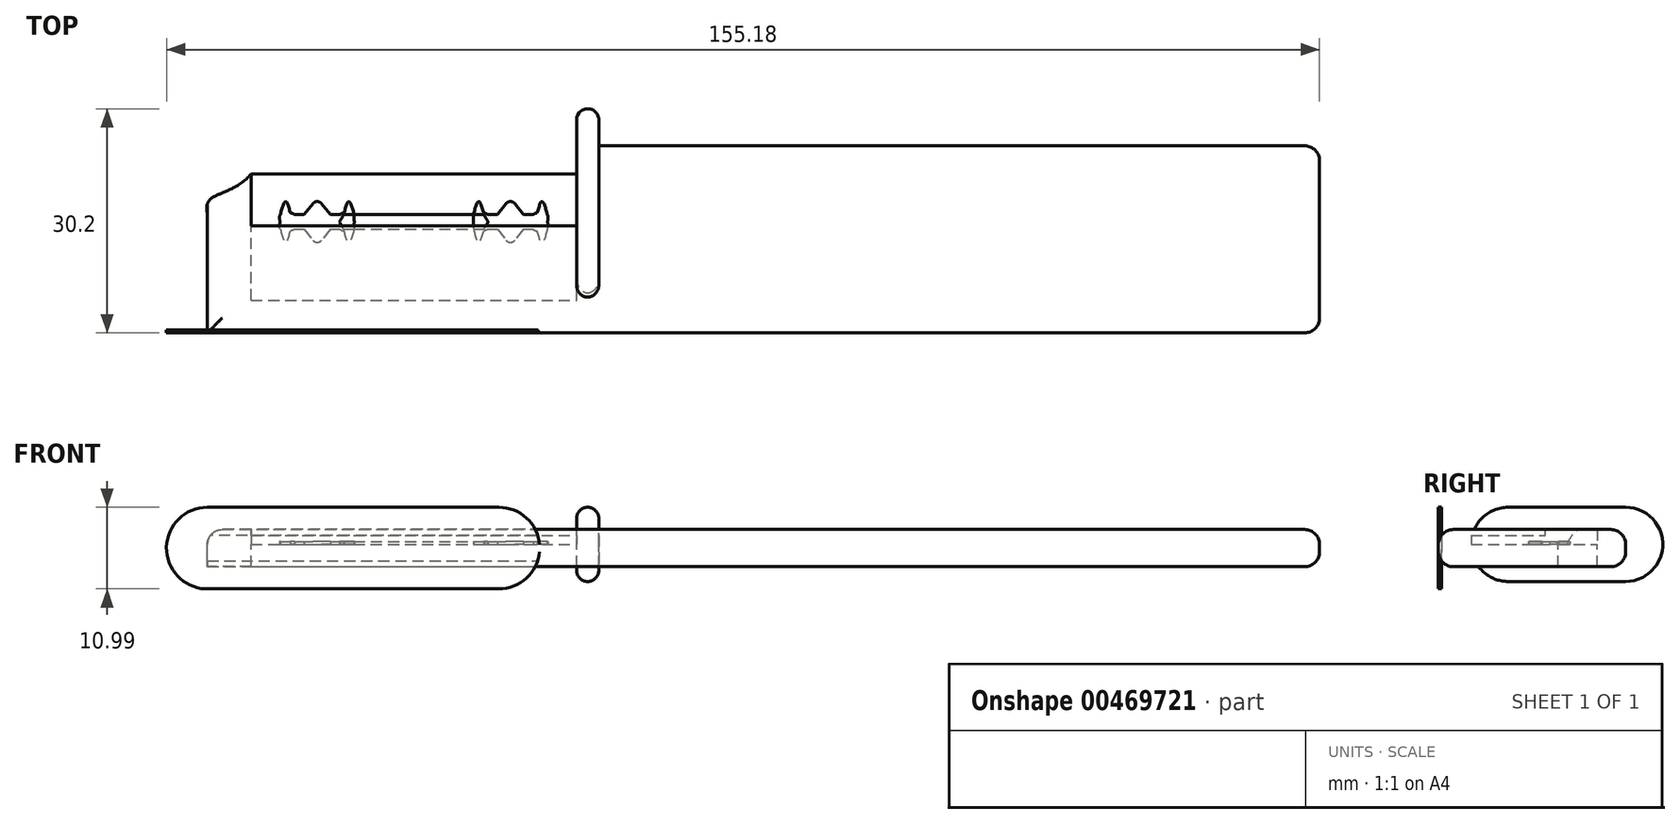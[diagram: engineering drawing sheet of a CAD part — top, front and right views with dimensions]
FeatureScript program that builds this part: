
annotation { "Feature Type Name" : "Feature", "Feature Type Description" : "" }
export const myFeature = defineFeature(function(context is Context, id is Id, definition is map)
    precondition{}
    {
        {
            var Q0;
            Q0=qCreatedBy(makeId("Top.planeOp"),FACE);
            var sketch = newSketch(context, id + "F0", { "sketchPlane" : qUnion([Q0])});
            skLineSegment(sketch, "E0", {"start": v(-36, 0) * mm, "end": v(0, 0) * mm});
            skLineSegment(sketch, "E1", {"start": v(-36, 1) * mm, "end": v(0, 1) * mm});
            skLineSegment(sketch, "E2.MirrorCS", {"start": v(-36, 2) * mm, "end": v(0, 2) * mm});
            skPoint(sketch, "E3", {"position": v(-31, 3.75) * mm});
            skPoint(sketch, "E4.MirrorP", {"position": v(-31, -1.75) * mm});
            skLineSegment(sketch, "E5", {"start": v(-31, 3.75) * mm, "end": v(-31, -1.75) * mm});
            skArc(sketch, "E6", {"start": v(-30.41, 3.47) * mm, "mid": v(-31, 3.75) * mm, "end": v(-31.59, 3.47) * mm});
            skLineSegment(sketch, "E7", {"start": v(-32.75, 2) * mm, "end": v(-31.59, 3.47) * mm});
            skPoint(sketch, "E8", {"position": v(-31.59, 3.47) * mm});
            skPoint(sketch, "E9", {"position": v(-30.41, 3.47) * mm});
            skLineSegment(sketch, "E10", {"start": v(-18, -5.38) * mm, "end": v(-18, 16.22) * mm});
            skFitSpline(sketch, "E11", {"points": [v(-35.93, 2) * mm, v(-35.23, 3.75) * mm, v(-34.53, 2) * mm, v(-34, 1) * mm, v(-34.07, 0) * mm, v(-35.93, 0) * mm, v(-36, 1) * mm, v(-35.93, 2) * mm]});
            skFitSpline(sketch, "E12.MirrorCS", {"points": [v(-35.93, 0) * mm, v(-35.23, -1.75) * mm, v(-34.53, 0) * mm, v(-34, 1) * mm, v(-34.07, 2) * mm, v(-35.93, 2) * mm, v(-36, 1) * mm, v(-35.93, 0) * mm]});
            skLineSegment(sketch, "E13.MirrorCS", {"start": v(-29.25, 2) * mm, "end": v(-30.41, 3.47) * mm});
            skLineSegment(sketch, "E14.MirrorCS", {"start": v(-32.75, 0) * mm, "end": v(-31.59, -1.47) * mm});
            skArc(sketch, "E15.MirrorCS", {"start": v(-30.41, -1.47) * mm, "mid": v(-31, -1.75) * mm, "end": v(-31.59, -1.47) * mm});
            skLineSegment(sketch, "E16.MirrorCS", {"start": v(-29.25, 0) * mm, "end": v(-30.41, -1.47) * mm});
            skFitSpline(sketch, "E17.MirrorCS", {"points": [v(-26.07, 2) * mm, v(-26.77, 3.75) * mm, v(-27.47, 2) * mm, v(-28, 1) * mm, v(-27.93, 0) * mm, v(-26.07, 0) * mm, v(-26, 1) * mm, v(-26.07, 2) * mm]});
            skFitSpline(sketch, "E18.MirrorCS", {"points": [v(-26.07, 0) * mm, v(-26.77, -1.75) * mm, v(-27.47, 0) * mm, v(-28, 1) * mm, v(-27.93, 2) * mm, v(-26.07, 2) * mm, v(-26, 1) * mm, v(-26.07, 0) * mm]});
            skFitSpline(sketch, "E19.MirrorCS", {"points": [v(-0.07, 2) * mm, v(-0.77, 3.75) * mm, v(-1.47, 2) * mm, v(-2, 1) * mm, v(-1.93, 0) * mm, v(-0.07, 0) * mm, v(0, 1) * mm, v(-0.07, 2) * mm]});
            skFitSpline(sketch, "E20.MirrorCS", {"points": [v(-0.07, 0) * mm, v(-0.77, -1.75) * mm, v(-1.47, 0) * mm, v(-2, 1) * mm, v(-1.93, 2) * mm, v(-0.07, 2) * mm, v(0, 1) * mm, v(-0.07, 0) * mm]});
            skLineSegment(sketch, "E21.MirrorCS", {"start": v(-3.25, 2) * mm, "end": v(-4.41, 3.47) * mm});
            skArc(sketch, "E22.MirrorCS", {"start": v(-5.59, 3.47) * mm, "mid": v(-5, 3.75) * mm, "end": v(-4.41, 3.47) * mm});
            skArc(sketch, "E23.MirrorCS", {"start": v(-5.59, -1.47) * mm, "mid": v(-5, -1.75) * mm, "end": v(-4.41, -1.47) * mm});
            skLineSegment(sketch, "E24.MirrorCS", {"start": v(-3.25, 0) * mm, "end": v(-4.41, -1.47) * mm});
            skLineSegment(sketch, "E25.MirrorCS", {"start": v(-6.75, 2) * mm, "end": v(-5.59, 3.47) * mm});
            skLineSegment(sketch, "E26.MirrorCS", {"start": v(-6.75, 0) * mm, "end": v(-5.59, -1.47) * mm});
            skFitSpline(sketch, "E27.MirrorCS", {"points": [v(-9.93, 2) * mm, v(-9.23, 3.75) * mm, v(-8.53, 2) * mm, v(-8, 1) * mm, v(-8.07, 0) * mm, v(-9.93, 0) * mm, v(-10, 1) * mm, v(-9.93, 2) * mm]});
            skFitSpline(sketch, "E28.MirrorCS", {"points": [v(-9.93, 0) * mm, v(-9.23, -1.75) * mm, v(-8.53, 0) * mm, v(-8, 1) * mm, v(-8.07, 2) * mm, v(-9.93, 2) * mm, v(-10, 1) * mm, v(-9.93, 0) * mm]});
            skSolve(sketch);
        }
        {
            var Q0;
            Q0 = qSketchRegion(id + "F0", true);
            extrude(context, id + "F1", {"entities" : qUnion([Q0]), "depth" : .4 * mm, "offsetDistance" : 25 * mm});
        }
        {
            var Q0;
            Q0=makeQuery(id+"F1.opExtrude","CAP_FACE",FACE,{"disambiguationData":[OSD([sQuery(id+"F0.wireOp",EDGE,"E0"),sQuery(id+"F0.wireOp",EDGE,"E2.MirrorCS"),sQuery(id+"F0.wireOp",EDGE,"E6"),sQuery(id+"F0.wireOp",EDGE,"E7"),sQuery(id+"F0.wireOp",EDGE,"E11"),sQuery(id+"F0.wireOp",EDGE,"E12.MirrorCS"),sQuery(id+"F0.wireOp",EDGE,"E13.MirrorCS"),sQuery(id+"F0.wireOp",EDGE,"E14.MirrorCS"),sQuery(id+"F0.wireOp",EDGE,"E15.MirrorCS"),sQuery(id+"F0.wireOp",EDGE,"E16.MirrorCS"),sQuery(id+"F0.wireOp",EDGE,"E17.MirrorCS"),sQuery(id+"F0.wireOp",EDGE,"E18.MirrorCS"),sQuery(id+"F0.wireOp",EDGE,"E19.MirrorCS"),sQuery(id+"F0.wireOp",EDGE,"E20.MirrorCS"),sQuery(id+"F0.wireOp",EDGE,"E21.MirrorCS"),sQuery(id+"F0.wireOp",EDGE,"E22.MirrorCS"),sQuery(id+"F0.wireOp",EDGE,"E23.MirrorCS"),sQuery(id+"F0.wireOp",EDGE,"E24.MirrorCS"),sQuery(id+"F0.wireOp",EDGE,"E25.MirrorCS"),sQuery(id+"F0.wireOp",EDGE,"E26.MirrorCS"),sQuery(id+"F0.wireOp",EDGE,"E27.MirrorCS"),sQuery(id+"F0.wireOp",EDGE,"E28.MirrorCS")])],"isStart":true});
            var sketch = newSketch(context, id + "F2", { "sketchPlane" : qUnion([Q0])});
            skLineSegment(sketch, "E29", {"start": v(-39.9, -7.45) * mm, "end": v(3.9, -7.45) * mm});
            skLineSegment(sketch, "E30", {"start": v(-39.9, 9.55) * mm, "end": v(3.9, 9.55) * mm});
            skLineSegment(sketch, "E31", {"start": v(-39.9, 9.55) * mm, "end": v(-39.9, -7.45) * mm});
            skLineSegment(sketch, "E32", {"start": v(3.9, 9.55) * mm, "end": v(3.9, -7.45) * mm});
            skLineSegment(sketch, "E33", {"start": v(3.9, -11.25) * mm, "end": v(103.9, -11.25) * mm});
            skLineSegment(sketch, "E34", {"start": v(-39.6, 13.55) * mm, "end": v(103.9, 13.55) * mm});
            skLineSegment(sketch, "E35", {"start": v(103.9, -11.25) * mm, "end": v(103.9, 13.55) * mm});
            skLineSegment(sketch, "E36", {"start": v(-39.6, 13.55) * mm, "end": v(-45.78, 13.55) * mm});
            skLineSegment(sketch, "E37", {"start": v(-45.78, 13.55) * mm, "end": v(-45.78, -3.45) * mm});
            skFitSpline(sketch, "E38", {"points": [v(-39.9, -7.45) * mm, v(-45.78, -3.45) * mm, v(-39.9, 5.9) * mm], "startDerivative": vector(-14.74, 17.67) * mm, "endDerivative": vector(17.5, 14.8) * mm});
            skLineSegment(sketch, "E39", {"start": v(3.9, -7.45) * mm, "end": v(3.9, -11.25) * mm});
            skSolve(sketch);
        }
        {
            var Q0;
            Q0 = qSketchRegion(id + "F2", true);
            extrude(context, id + "F3", {"entities" : qUnion([Q0]), "operationType" : NewBodyOperationType.ADD, "depth" : 3 * mm});
        }
        {
            var Q0;
            Q0=makeQuery(id+"F2.imprint","IMPRINT",FACE,{"disambiguationData":[TD([[makeQuery(id+"F2.imprint","IMPRINT",EDGE,{"derivedFrom":sQuery(id+"F2.wireOp",EDGE,"E30")}),1.0]])]});
            var Q1;
            Q1=makeQuery(id+"F2.imprint","IMPRINT",FACE,{"disambiguationData":[TD([[makeQuery(id+"F2.imprint","IMPRINT",EDGE,{"derivedFrom":sQuery(id+"F2.wireOp",EDGE,"E31")}),-1.0]])]});
            extrude(context, id + "F4", {"entities" : qUnion([Q0, Q1]), "operationType" : NewBodyOperationType.ADD, "oppositeDirection" : true, "depth" : 2 * mm});
        }
        {
            var Q0;
            Q0=makeQuery(id+"F4.opExtrude","CAP_FACE",FACE,{"disambiguationData":[OSD([sQuery(id+"F2.wireOp",EDGE,"E30"),sQuery(id+"F2.wireOp",EDGE,"E31"),sQuery(id+"F2.wireOp",EDGE,"E32"),sQuery(id+"F2.wireOp",EDGE,"E33"),sQuery(id+"F2.wireOp",EDGE,"8b2e560c-d758-45f4-89a4-b663eee040c1"),sQuery(id+"F2.wireOp",EDGE,"E34"),sQuery(id+"F2.wireOp",EDGE,"E35"),sQuery(id+"F2.wireOp",EDGE,"E36"),sQuery(id+"F2.wireOp",EDGE,"E37"),sQuery(id+"F2.wireOp",EDGE,"c306e02f-bcff-4e16-9162-90af26744d23")])],"isStart":false});
            var sketch = newSketch(context, id + "F5", { "sketchPlane" : qUnion([Q0])});
            skLineSegment(sketch, "E40.bottom", {"start": v(3.9, -9.55) * mm, "end": v(-39.9, -9.55) * mm});
            skLineSegment(sketch, "E40.top", {"start": v(3.9, 0.45) * mm, "end": v(-39.9, 0.45) * mm});
            skLineSegment(sketch, "E40.left", {"start": v(3.9, -9.55) * mm, "end": v(3.9, 0.45) * mm});
            skLineSegment(sketch, "E40.right", {"start": v(-39.9, -9.55) * mm, "end": v(-39.9, 0.45) * mm});
            skSolve(sketch);
        }
        {
            var Q0;
            Q0 = qSketchRegion(id + "F5", true);
            extrude(context, id + "F6", {"entities" : qUnion([Q0]), "operationType" : NewBodyOperationType.ADD, "oppositeDirection" : true, "depth" : .8 * mm});
        }
        {
            var Q0;
            {var subQ0=sQuery(id+"F2.wireOp",EDGE,"E36");var subQ1=sQuery(id+"F2.wireOp",EDGE,"E34");Q0=makeQuery(id+"F4.boolean.opBoolean","MERGE",FACE,{"derivedFrom":[makeQuery(id+"F3.opExtrude","SWEPT_FACE",FACE,{"disambiguationData":[OSD([subQ1,subQ0])]}),makeQuery(id+"F4.opExtrude","SWEPT_FACE",FACE,{"disambiguationData":[OSD([subQ1,subQ0])]})]});}
            var sketch = newSketch(context, id + "F7", { "sketchPlane" : qUnion([Q0])});
            skLineSegment(sketch, "E41.bottom", {"start": v(-45.78, 2) * mm, "end": v(103.9, 2) * mm});
            skLineSegment(sketch, "E41.top", {"start": v(-45.78, -3) * mm, "end": v(103.9, -3) * mm});
            skLineSegment(sketch, "E41.left", {"start": v(-45.78, 2) * mm, "end": v(-45.78, -3) * mm});
            skLineSegment(sketch, "E41.right", {"start": v(103.9, 2) * mm, "end": v(103.9, -3) * mm});
            skLineSegment(sketch, "E42", {"start": v(-6.54, 5) * mm, "end": v(-45.78, 5) * mm});
            skLineSegment(sketch, "E43.MirrorCS", {"start": v(-6.54, -6) * mm, "end": v(-46.03, -6) * mm});
            skArc(sketch, "E44", {"start": v(-45.78, 5) * mm, "mid": v(-51.28, -0.38) * mm, "end": v(-46.03, -6) * mm});
            skArc(sketch, "E45", {"start": v(-6.54, -6) * mm, "mid": v(-3.67, -5.19) * mm, "end": v(-1.65, -3) * mm});
            skArc(sketch, "E46.trimOffspring", {"start": v(-1.65, 2) * mm, "mid": v(-3.67, 4.2) * mm, "end": v(-6.54, 5) * mm});
            skSolve(sketch);
        }
        {
            var Q0;
            Q0 = qSketchRegion(id + "F7", true);
            extrude(context, id + "F8", {"entities" : qUnion([Q0]), "operationType" : NewBodyOperationType.ADD, "depth" : .4 * mm});
        }
        {
            var Q0;
            {var subQ0=sQuery(id+"F2.wireOp",EDGE,"E35");var subQ1=sQuery(id+"F2.wireOp",EDGE,"E33");Q0=makeQuery(id+"F4.boolean.opBoolean","MERGE",EDGE,{"derivedFrom":[makeQuery(id+"F3.opExtrude","SWEPT_EDGE",EDGE,{"disambiguationData":[OSD([subQ1,subQ0])]}),makeQuery(id+"F4.opExtrude","SWEPT_EDGE",EDGE,{"disambiguationData":[OSD([subQ1,subQ0])]})]});}
            fillet(context, id + "F9", {"entities" : qUnion([Q0]), "radius" : 2 * mm, "tangentPropagation" : true, "allowEdgeOverflow" : false});
        }
        {
            var Q0;
            Q0=makeQuery(id+"F8.opExtrude","CAP_EDGE",EDGE,{"disambiguationData":[OSD([sQuery(id+"F7.wireOp",EDGE,"E41.right")])],"isStart":false});
            fillet(context, id + "F10", {"entities" : qUnion([Q0]), "radius" : 2 * mm, "tangentPropagation" : true, "allowEdgeOverflow" : false});
        }
        {
            var Q0;
            Q0=makeQuery(id+"F4.opExtrude","CAP_EDGE",EDGE,{"disambiguationData":[OSD([sQuery(id+"F2.wireOp",EDGE,"E33")])],"isStart":false});
            fillet(context, id + "F11", {"entities" : qUnion([Q0]), "radius" : 2 * mm, "tangentPropagation" : true, "allowEdgeOverflow" : false});
        }
        {
            var Q0;
            Q0=makeQuery(id+"F3.opExtrude","CAP_EDGE",EDGE,{"disambiguationData":[OSD([sQuery(id+"F2.wireOp",EDGE,"E33")])],"isStart":false});
            fillet(context, id + "F12", {"entities" : qUnion([Q0]), "radius" : 2 * mm, "tangentPropagation" : true, "allowEdgeOverflow" : false});
        }
        {
            var Q0;
            Q0=makeQuery(id+"F4.opExtrude","CAP_EDGE",EDGE,{"disambiguationData":[OSD([sQuery(id+"F2.wireOp",EDGE,"E37")])],"isStart":false});
            fillet(context, id + "F13", {"entities" : qUnion([Q0]), "radius" : 2 * mm, "tangentPropagation" : true, "allowEdgeOverflow" : false});
        }
        {
            var Q0;
            {var subQ0=sQuery(id+"F2.wireOp",EDGE,"E39");Q0=makeQuery(id+"F4.boolean.opBoolean","MERGE",FACE,{"derivedFrom":[makeQuery(id+"F3.opExtrude","SWEPT_FACE",FACE,{"disambiguationData":[OSD([subQ0])]}),makeQuery(id+"F4.opExtrude","SWEPT_FACE",FACE,{"disambiguationData":[OSD([sQuery(id+"F2.wireOp",EDGE,"E32"),subQ0])]})]});}
            var sketch = newSketch(context, id + "F14", { "sketchPlane" : qUnion([Q0])});
            skLineSegment(sketch, "E47", {"start": v(-11.25, 0) * mm, "end": v(-16.25, 0) * mm});
            skLineSegment(sketch, "E48", {"start": v(-16.25, 0) * mm, "end": v(-16.25, 0) * mm});
            skLineSegment(sketch, "E49", {"start": v(-11.25, -5) * mm, "end": v(4.55, -5) * mm});
            skLineSegment(sketch, "E50", {"start": v(9.55, 0) * mm, "end": v(9.55, 0) * mm});
            skPoint(sketch, "E51.visualSharp", {"position": v(9.55, -5) * mm});
            skArc(sketch, "E51.filletArc", {"start": v(4.55, -5) * mm, "mid": v(8.09, -3.54) * mm, "end": v(9.55, 0) * mm});
            skPoint(sketch, "E52.visualSharp", {"position": v(-16.25, -5) * mm});
            skArc(sketch, "E52.filletArc", {"start": v(-16.25, 0) * mm, "mid": v(-14.79, -3.54) * mm, "end": v(-11.25, -5) * mm});
            skLineSegment(sketch, "E53.MirrorCS", {"start": v(-11.25, 5) * mm, "end": v(4.55, 5) * mm});
            skArc(sketch, "E54.MirrorCS", {"start": v(4.55, 5) * mm, "mid": v(8.09, 3.54) * mm, "end": v(9.55, 0) * mm});
            skArc(sketch, "E55.MirrorCS", {"start": v(-16.25, 0) * mm, "mid": v(-14.79, 3.54) * mm, "end": v(-11.25, 5) * mm});
            skSolve(sketch);
        }
        {
            var Q0;
            Q0=makeQuery(id+"F14.imprint","IMPRINT",FACE,{"disambiguationData":[TD([[makeQuery(id+"F14.imprint","IMPRINT",EDGE,{"derivedFrom":sQuery(id+"F14.wireOp",EDGE,"E47")}),-1.0]])]});
            var Q1;
            Q1=makeQuery(id+"F14.imprint","IMPRINT",FACE,{"disambiguationData":[TD([[makeQuery(id+"F14.imprint","IMPRINT",EDGE,{"derivedFrom":sQuery(id+"F14.wireOp",EDGE,"E47")}),1.0]])]});
            extrude(context, id + "F15", {"entities" : qUnion([Q0, Q1]), "operationType" : NewBodyOperationType.ADD, "depth" : -3 * mm, "offsetDistance" : 25 * mm});
        }
        {
            var Q0;
            Q0=makeQuery(id+"F15.opExtrude","CAP_EDGE",EDGE,{"disambiguationData":[OSD([sQuery(id+"F14.wireOp",EDGE,"E52.filletArc"),sQuery(id+"F14.wireOp",EDGE,"E55.MirrorCS")])],"isStart":false});
            var Q1;
            Q1=makeQuery(id+"F15.opExtrude","CAP_EDGE",EDGE,{"disambiguationData":[OSD([sQuery(id+"F14.wireOp",EDGE,"E52.filletArc"),sQuery(id+"F14.wireOp",EDGE,"E55.MirrorCS")])],"isStart":true});
            var Q2;
            Q2=makeQuery(id+"F15.opExtrude","CAP_EDGE",EDGE,{"disambiguationData":[OSD([sQuery(id+"F14.wireOp",EDGE,"E53.MirrorCS")])],"isStart":true});
            var Q3;
            Q3=makeQuery(id+"F15.opExtrude","CAP_EDGE",EDGE,{"disambiguationData":[OSD([sQuery(id+"F14.wireOp",EDGE,"E54.MirrorCS")])],"isStart":true});
            var Q4;
            Q4=makeQuery(id+"F15.opExtrude","CAP_EDGE",EDGE,{"disambiguationData":[OSD([sQuery(id+"F14.wireOp",EDGE,"E53.MirrorCS")])],"isStart":false});
            var Q5;
            Q5=makeQuery(id+"F15.opExtrude","CAP_EDGE",EDGE,{"disambiguationData":[OSD([sQuery(id+"F14.wireOp",EDGE,"E51.filletArc")])],"isStart":false});
            var Q6;
            Q6=makeQuery(id+"F15.opExtrude","CAP_EDGE",EDGE,{"disambiguationData":[OSD([sQuery(id+"F14.wireOp",EDGE,"E51.filletArc")])],"isStart":true});
            var Q7;
            Q7=makeQuery(id+"F15.opExtrude","CAP_EDGE",EDGE,{"disambiguationData":[OSD([sQuery(id+"F14.wireOp",EDGE,"E49")])],"isStart":true});
            var Q8;
            Q8=makeQuery(id+"F15.opExtrude","CAP_EDGE",EDGE,{"disambiguationData":[OSD([sQuery(id+"F14.wireOp",EDGE,"E49")])],"isStart":false});
            fillet(context, id + "F16", {"entities" : qUnion([Q0, Q1, Q2, Q3, Q4, Q5, Q6, Q7, Q8]), "radius" : 1.5 * mm, "tangentPropagation" : true, "allowEdgeOverflow" : false});
        }
    });
